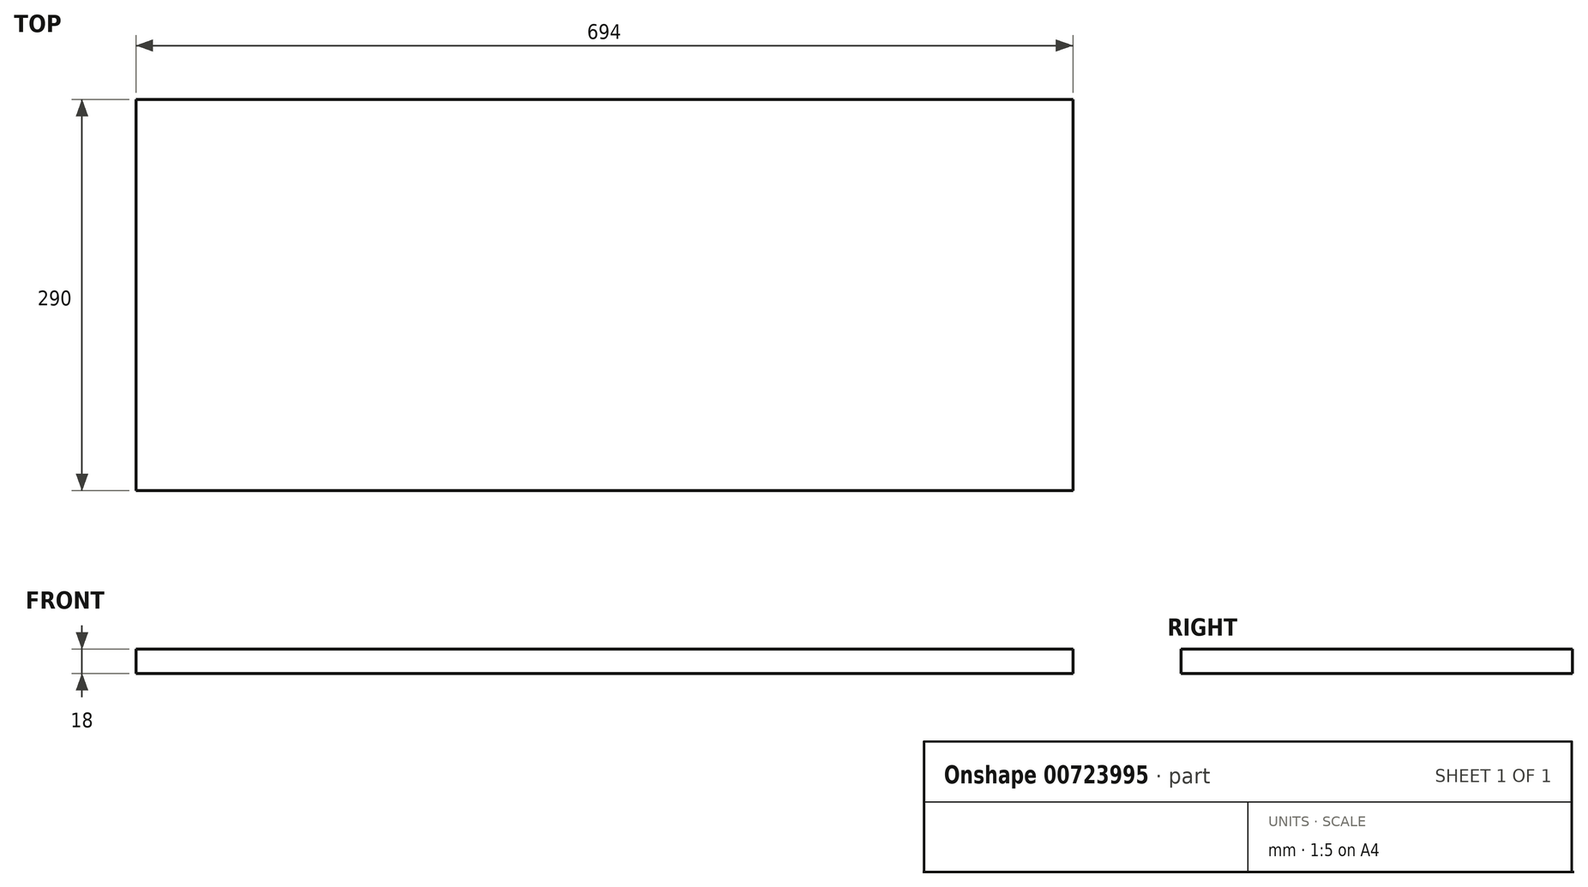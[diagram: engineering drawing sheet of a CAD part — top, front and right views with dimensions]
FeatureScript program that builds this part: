
annotation { "Feature Type Name" : "Feature", "Feature Type Description" : "" }
export const myFeature = defineFeature(function(context is Context, id is Id, definition is map)
    precondition{}
    {
        {
            var Q0;
            Q0=qCreatedBy(makeId("Top.planeOp"),FACE);
            var sketch = newSketch(context, id + "F0", { "sketchPlane" : qUnion([Q0])});
            skLineSegment(sketch, "E0.bottom", {"start": v(-347, 145) * mm, "end": v(347, 145) * mm});
            skLineSegment(sketch, "E0.top", {"start": v(-347, -145) * mm, "end": v(347, -145) * mm});
            skLineSegment(sketch, "E0.left", {"start": v(-347, 145) * mm, "end": v(-347, -145) * mm});
            skLineSegment(sketch, "E0.right", {"start": v(347, 145) * mm, "end": v(347, -145) * mm});
            skLineSegment(sketch, "E1", {"start": v(-347, 145) * mm, "end": v(347, -145) * mm, "construction": true});
            skLineSegment(sketch, "E2", {"start": v(347, 145) * mm, "end": v(-347, -145) * mm, "construction": true});
            skSolve(sketch);
        }
        {
            var Q0;
            Q0=qSketchRegion(id+"F0",true);
            extrude(context, id + "F1", {"entities" : qUnion([Q0]), "depth" : 18 * mm, "offsetDistance" : 25 * mm});
        }
    });
